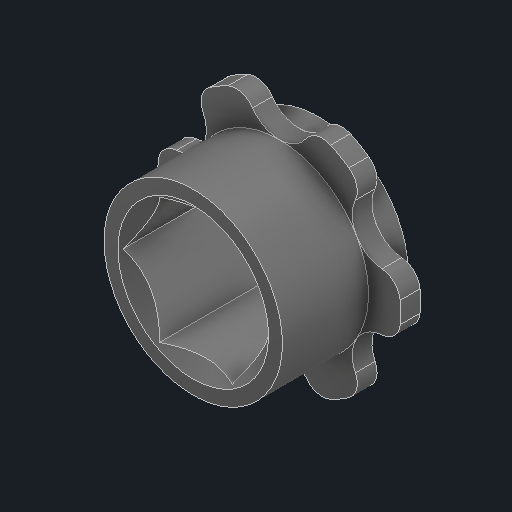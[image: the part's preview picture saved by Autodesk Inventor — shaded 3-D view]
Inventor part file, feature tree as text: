
AUTODESK INVENTOR PART (.ipt)
format: ipt  version: 2024 (Build 280153000, 153)  size: 181,760 bytes
history: native  units: in
note: dims shown in document units (in); Inventor stores cm internally (conversion verified against a paired STEP export)
features: fillet x1
ambient origin geometry x8: Origin, YZ Plane, XZ Plane, XY Plane, X Axis, Y Axis, Z Axis, Center Point
bodies: Solid1 (feature_tree)
feature tree (1):
  fillet  "Fillet1"  [1 undecoded]
note: 1 required parameter value undecoded (feature->parameter linkage not recoverable at this tier; creation-order binding heuristic only, values carry confidence <= 0.55)
